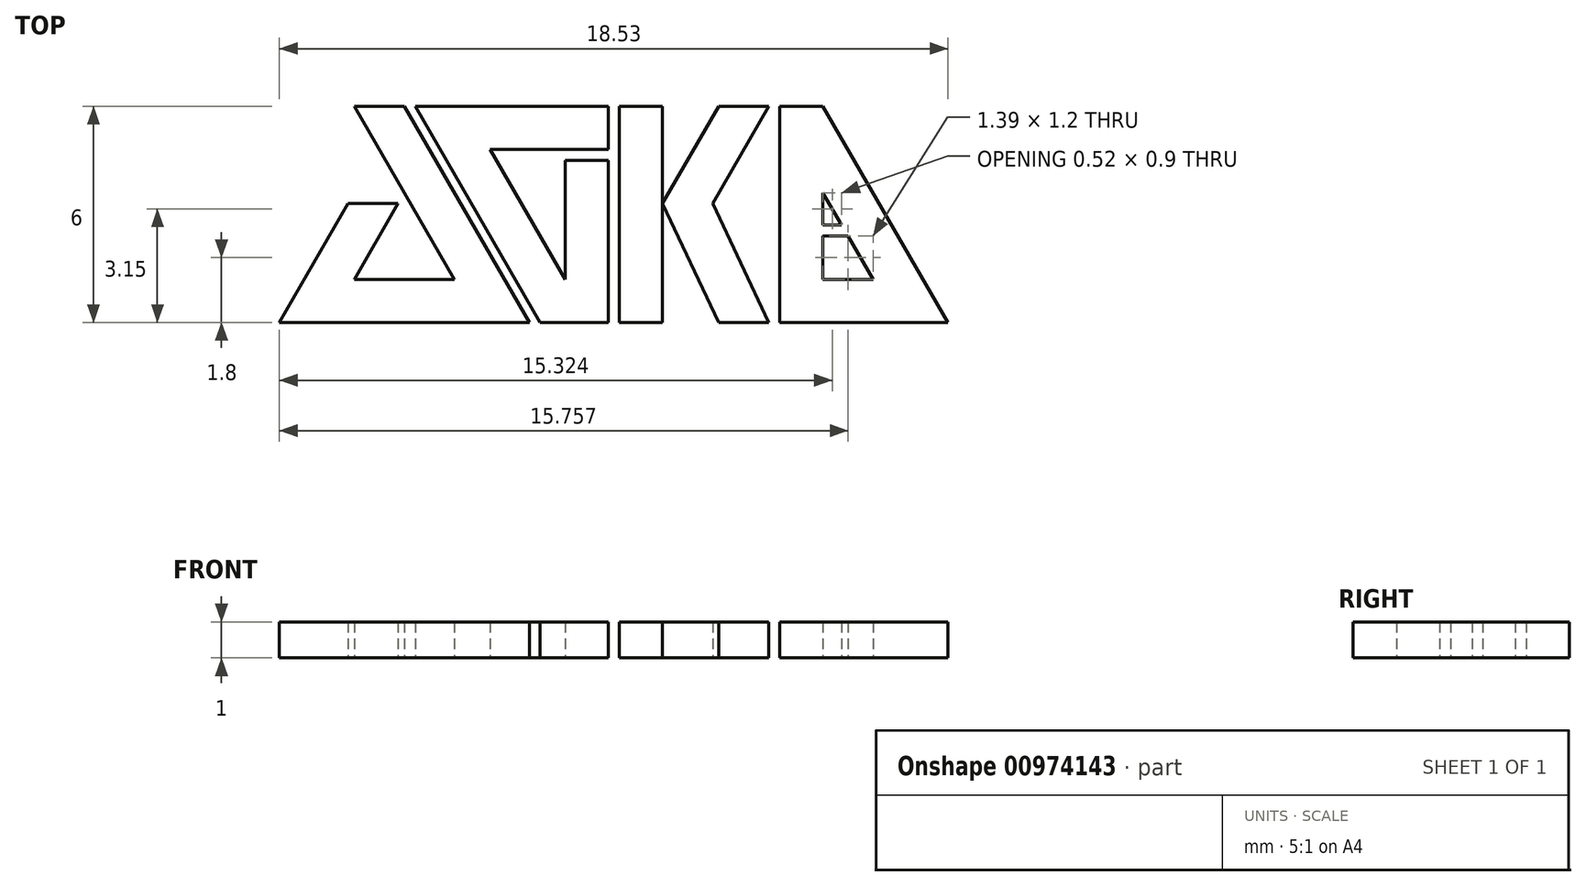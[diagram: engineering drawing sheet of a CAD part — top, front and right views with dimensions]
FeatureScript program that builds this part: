
annotation { "Feature Type Name" : "Feature", "Feature Type Description" : "" }
export const myFeature = defineFeature(function(context is Context, id is Id, definition is map)
    precondition{}
    {
        {
            var Q0;
            Q0=qCreatedBy(makeId("Top.planeOp"),FACE);
            var sketch = newSketch(context, id + "F0", { "sketchPlane" : qUnion([Q0])});
            skLineSegment(sketch, "E0", {"start": v(-7.04, 6) * mm, "end": v(-5.66, 6) * mm});
            skLineSegment(sketch, "E1", {"start": v(-5.66, 6) * mm, "end": v(-2.2, 0) * mm});
            skLineSegment(sketch, "E2", {"start": v(-2.2, 0) * mm, "end": v(-9.12, 0) * mm});
            skLineSegment(sketch, "E3", {"start": v(-9.12, 0) * mm, "end": v(-7.22, 3.3) * mm});
            skLineSegment(sketch, "E4", {"start": v(-7.22, 3.3) * mm, "end": v(-5.83, 3.3) * mm});
            skLineSegment(sketch, "E5", {"start": v(-5.83, 3.3) * mm, "end": v(-7.04, 1.2) * mm});
            skLineSegment(sketch, "E6", {"start": v(-7.04, 1.2) * mm, "end": v(-4.27, 1.2) * mm});
            skLineSegment(sketch, "E7", {"start": v(-4.27, 1.2) * mm, "end": v(-7.04, 6) * mm});
            skLineSegment(sketch, "E8", {"start": v(-5.36, 6) * mm, "end": v(-1.9, 0) * mm});
            skLineSegment(sketch, "E9", {"start": v(-1.9, 0) * mm, "end": v(0, 0) * mm});
            skLineSegment(sketch, "E10", {"start": v(0, 0) * mm, "end": v(0, 4.5) * mm});
            skLineSegment(sketch, "E11", {"start": v(0, 4.5) * mm, "end": v(-1.2, 4.5) * mm});
            skLineSegment(sketch, "E12", {"start": v(-1.2, 4.5) * mm, "end": v(-1.2, 1.2) * mm});
            skLineSegment(sketch, "E13", {"start": v(0, 6) * mm, "end": v(-5.36, 6) * mm});
            skLineSegment(sketch, "E14", {"start": v(-1.2, 1.2) * mm, "end": v(-3.28, 4.8) * mm});
            skLineSegment(sketch, "E15", {"start": v(-3.28, 4.8) * mm, "end": v(0, 4.8) * mm});
            skLineSegment(sketch, "E16", {"start": v(0, 4.8) * mm, "end": v(0, 6) * mm});
            skLineSegment(sketch, "E17", {"start": v(0.3, 6) * mm, "end": v(0.3, 0) * mm});
            skLineSegment(sketch, "E18", {"start": v(0.3, 0) * mm, "end": v(1.5, 0) * mm});
            skLineSegment(sketch, "E19", {"start": v(1.5, 0) * mm, "end": v(1.5, 3.3) * mm});
            skLineSegment(sketch, "E20", {"start": v(1.5, 3.3) * mm, "end": v(3.06, 0) * mm});
            skLineSegment(sketch, "E21", {"start": v(3.06, 0) * mm, "end": v(4.44, 0) * mm});
            skLineSegment(sketch, "E22", {"start": v(4.44, 0) * mm, "end": v(2.89, 3.3) * mm});
            skLineSegment(sketch, "E23", {"start": v(2.89, 3.3) * mm, "end": v(4.44, 6) * mm});
            skLineSegment(sketch, "E24", {"start": v(4.44, 6) * mm, "end": v(3.06, 6) * mm});
            skLineSegment(sketch, "E25", {"start": v(3.06, 6) * mm, "end": v(1.5, 3.3) * mm});
            skLineSegment(sketch, "E26", {"start": v(1.5, 3.3) * mm, "end": v(1.5, 6) * mm});
            skLineSegment(sketch, "E27", {"start": v(1.5, 6) * mm, "end": v(0.3, 6) * mm});
            skLineSegment(sketch, "E28", {"start": v(4.74, 6) * mm, "end": v(4.74, 0) * mm});
            skLineSegment(sketch, "E29", {"start": v(4.74, 0) * mm, "end": v(9.4, 0) * mm});
            skLineSegment(sketch, "E30", {"start": v(9.4, 0) * mm, "end": v(5.94, 6) * mm});
            skLineSegment(sketch, "E31", {"start": v(5.94, 6) * mm, "end": v(4.74, 6) * mm});
            skLineSegment(sketch, "E32", {"start": v(5.94, 3.6) * mm, "end": v(5.94, 2.7) * mm});
            skLineSegment(sketch, "E33", {"start": v(5.94, 2.7) * mm, "end": v(6.46, 2.7) * mm});
            skLineSegment(sketch, "E34", {"start": v(6.46, 2.7) * mm, "end": v(5.94, 3.6) * mm});
            skLineSegment(sketch, "E35", {"start": v(5.94, 2.4) * mm, "end": v(5.94, 1.2) * mm});
            skLineSegment(sketch, "E36", {"start": v(5.94, 1.2) * mm, "end": v(7.33, 1.2) * mm});
            skLineSegment(sketch, "E37", {"start": v(7.33, 1.2) * mm, "end": v(6.64, 2.4) * mm});
            skLineSegment(sketch, "E38", {"start": v(6.64, 2.4) * mm, "end": v(5.94, 2.4) * mm});
            skLineSegment(sketch, "E39.bottom", {"start": v(10.8, -1.9) * mm, "end": v(-11, -1.9) * mm, "construction": true});
            skLineSegment(sketch, "E39.top", {"start": v(10.8, 16.15) * mm, "end": v(-11, 16.15) * mm, "construction": true});
            skLineSegment(sketch, "E39.left", {"start": v(10.8, -1.9) * mm, "end": v(10.8, 16.15) * mm, "construction": true});
            skLineSegment(sketch, "E39.right", {"start": v(-11, -1.9) * mm, "end": v(-11, 16.15) * mm, "construction": true});
            skSolve(sketch);
        }
        {
            var Q0;
            Q0 = qSketchRegion(id + "F0", true);
            extrude(context, id + "F1", {"entities" : qUnion([Q0]), "depth" : 1 * mm, "offsetDistance" : 25 * mm});
        }
    });
